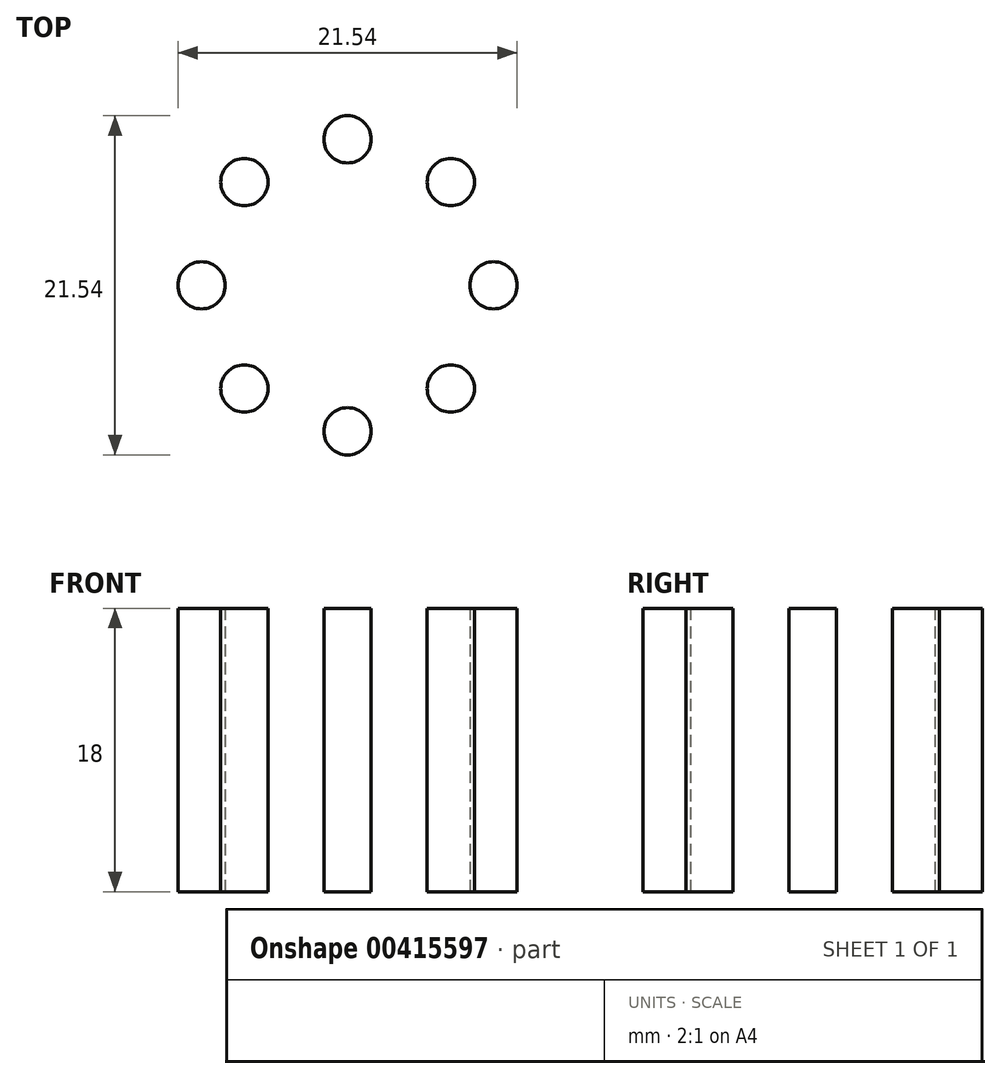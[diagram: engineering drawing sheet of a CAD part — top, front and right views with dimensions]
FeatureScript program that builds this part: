
annotation { "Feature Type Name" : "Feature", "Feature Type Description" : "" }
export const myFeature = defineFeature(function(context is Context, id is Id, definition is map)
    precondition{}
    {
        {
            var Q0;
            Q0=qCreatedBy(makeId("Top.planeOp"),FACE);
            var sketch = newSketch(context, id + "F0", { "sketchPlane" : qUnion([Q0])});
            skCircle(sketch, "E0", {"center": v(0, 9.27) * mm, "radius": 1.5 * mm});
            skSolve(sketch);
        }
        {
            var Q0;
            Q0=makeQuery(id+"F0.imprint","IMPRINT",FACE,{"disambiguationData":[TD([[makeQuery(id+"F0.imprint","IMPRINT",EDGE,{"derivedFrom":sQuery(id+"F0.wireOp",EDGE,"E0")}),1.0]])]});
            extrude(context, id + "F1", {"entities" : qUnion([Q0]), "depth" : 18 * mm});
        }
        {
            var Q0;
            Q0=qCreatedBy(makeId("Front.planeOp"),FACE);
            var sketch = newSketch(context, id + "F2", { "sketchPlane" : qUnion([Q0])});
            skLineSegment(sketch, "E1", {"start": v(0, 0) * mm, "end": v(0, 55) * mm, "construction": true});
            skSolve(sketch);
        }
        {
            var Q0;
            Q0=makeQuery(id+"F1.opExtrude","SWEPT_BODY",BODY,{"disambiguationData":[OSD([sQuery(id+"F0.wireOp",EDGE,"E0")])]});
            var Q1;
            Q1=sQuery(id+"F2.wireOp",EDGE,"E1");
            circularPattern(context, id + "F3", {"entities" : qUnion([Q0]), "axis" : qUnion([Q1]), "angle" : 360 * degree, "instanceCount" : 8, "equalSpace" : true});
        }
    });
